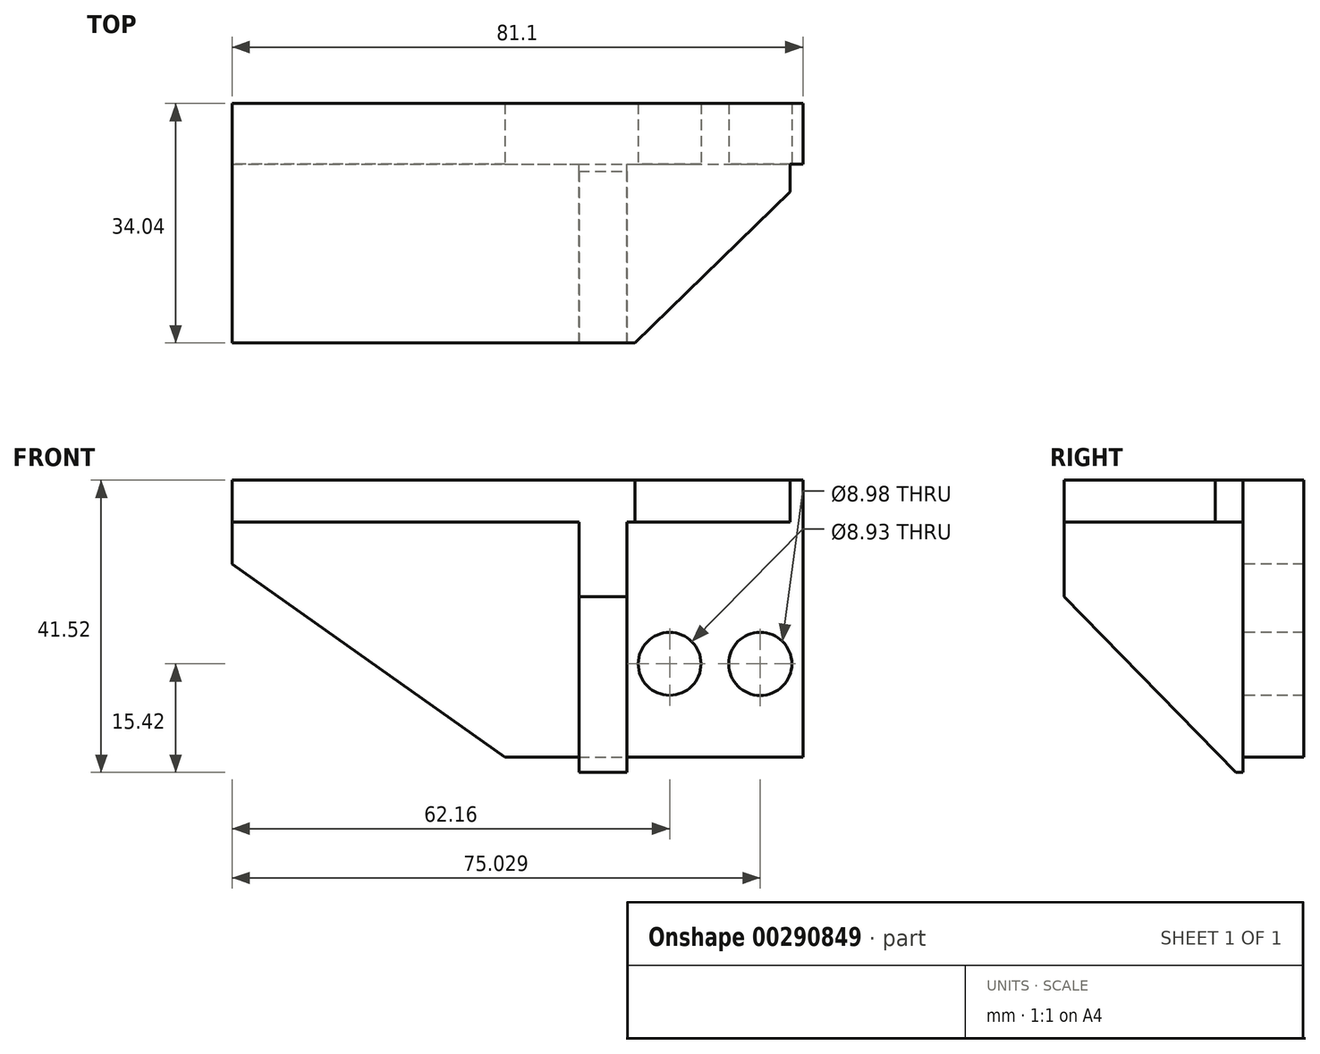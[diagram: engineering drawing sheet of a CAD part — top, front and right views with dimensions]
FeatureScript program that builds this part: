
annotation { "Feature Type Name" : "Feature", "Feature Type Description" : "" }
export const myFeature = defineFeature(function(context is Context, id is Id, definition is map)
    precondition{}
    {
        {
            var Q0;
            Q0=qCreatedBy(makeId("Front.planeOp"),FACE);
            var sketch = newSketch(context, id + "F0", { "sketchPlane" : qUnion([Q0])});
            skLineSegment(sketch, "E0.bottom", {"start": v(-49.3, 26.1) * mm, "end": v(31.8, 26.1) * mm});
            skLineSegment(sketch, "E0.top", {"start": v(-49.3, -13.23) * mm, "end": v(31.8, -13.23) * mm});
            skLineSegment(sketch, "E0.left", {"start": v(-49.3, 26.1) * mm, "end": v(-49.3, -13.23) * mm});
            skLineSegment(sketch, "E0.right", {"start": v(31.8, 26.1) * mm, "end": v(31.8, -13.23) * mm});
            skSolve(sketch);
        }
        {
            var Q0;
            Q0 = qSketchRegion(id + "F0", true);
            extrude(context, id + "F1", {"entities" : qUnion([Q0]), "depth" : 8.64 * mm});
        }
        {
            var Q0;
            Q0=makeQuery(id+"F1.opExtrude","CAP_FACE",FACE,{"disambiguationData":[OSD([sQuery(id+"F0.wireOp",EDGE,"E0.bottom"),sQuery(id+"F0.wireOp",EDGE,"E0.top"),sQuery(id+"F0.wireOp",EDGE,"E0.left"),sQuery(id+"F0.wireOp",EDGE,"E0.right")])],"isStart":false});
            var sketch = newSketch(context, id + "F2", { "sketchPlane" : qUnion([Q0])});
            skLineSegment(sketch, "E1", {"start": v(-8.62, -14.57) * mm, "end": v(-51.6, 15.78) * mm});
            skSolve(sketch);
        }
        {
            var Q0;
            {var subQ0=sQuery(id+"F2.wireOp",EDGE,"E1");var subQ1=makeQuery(id+"F1.opExtrude","CAP_EDGE",EDGE,{"disambiguationData":[OSD([sQuery(id+"F0.wireOp",EDGE,"E0.top")])],"isStart":false});var subQ2=makeQuery(id+"F2.imprint","INTERSECT",VERTEX,{"derivedFrom":[subQ1,subQ0]});Q0=makeQuery(id+"F2.imprint","IMPRINT",FACE,{"disambiguationData":[TD([[makeQuery(id+"F2.imprint","IMPRINT",EDGE,{"disambiguationData":[TD([[subQ2,-1.0]])],"derivedFrom":subQ0}),1.0]])]});}
            extrude(context, id + "F3", {"entities" : qUnion([Q0]), "operationType" : NewBodyOperationType.REMOVE, "oppositeDirection" : true, "depth" : 25.4 * mm});
        }
        {
            var Q0;
            Q0=makeQuery(id+"F1.opExtrude","CAP_FACE",FACE,{"disambiguationData":[OSD([sQuery(id+"F0.wireOp",EDGE,"E0.bottom"),sQuery(id+"F0.wireOp",EDGE,"E0.top"),sQuery(id+"F0.wireOp",EDGE,"E0.left"),sQuery(id+"F0.wireOp",EDGE,"E0.right")])],"isStart":false});
            var sketch = newSketch(context, id + "F4", { "sketchPlane" : qUnion([Q0])});
            skLineSegment(sketch, "E2", {"start": v(-50.14, 20.15) * mm, "end": v(29.99, 20.15) * mm});
            skLineSegment(sketch, "E3", {"start": v(29.99, 20.15) * mm, "end": v(29.99, 26.47) * mm});
            skLineSegment(sketch, "E4", {"start": v(29.99, 26.47) * mm, "end": v(-50.14, 26.47) * mm});
            skLineSegment(sketch, "E5", {"start": v(-50.14, 26.47) * mm, "end": v(-50.14, 20.15) * mm});
            skSolve(sketch);
        }
        {
            var Q0;
            {var subQ5=makeQuery(id+"F1.opExtrude","CAP_EDGE",EDGE,{"disambiguationData":[OSD([sQuery(id+"F0.wireOp",EDGE,"E0.bottom")])],"isStart":false});Q0=makeQuery(id+"F4.imprint","IMPRINT",FACE,{"disambiguationData":[TD([[makeQuery(id+"F4.imprint","IMPRINT",EDGE,{"derivedFrom":subQ5}),-1.0]])]});}
            extrude(context, id + "F5", {"entities" : qUnion([Q0]), "operationType" : NewBodyOperationType.ADD, "depth" : 25.4 * mm});
        }
        {
            var Q0;
            Q0=makeQuery(id+"F1.opExtrude","CAP_FACE",FACE,{"disambiguationData":[OSD([sQuery(id+"F0.wireOp",EDGE,"E0.bottom"),sQuery(id+"F0.wireOp",EDGE,"E0.top"),sQuery(id+"F0.wireOp",EDGE,"E0.left"),sQuery(id+"F0.wireOp",EDGE,"E0.right")])],"isStart":false});
            var sketch = newSketch(context, id + "F6", { "sketchPlane" : qUnion([Q0])});
            skLineSegment(sketch, "E6", {"start": v(0, 20.15) * mm, "end": v(0, -15.42) * mm});
            skLineSegment(sketch, "E7", {"start": v(0, -15.42) * mm, "end": v(6.8, -15.42) * mm});
            skLineSegment(sketch, "E8", {"start": v(6.8, -15.42) * mm, "end": v(6.8, 20.15) * mm});
            skLineSegment(sketch, "E9", {"start": v(6.8, 20.15) * mm, "end": v(0, 20.15) * mm});
            skSolve(sketch);
        }
        {
            var Q0;
            Q0 = qSketchRegion(id + "F6", true);
            extrude(context, id + "F7", {"entities" : qUnion([Q0]), "operationType" : NewBodyOperationType.ADD, "depth" : 25.4 * mm});
        }
        {
            var Q0;
            Q0=makeQuery(id+"F7.opExtrude","SWEPT_FACE",FACE,{"disambiguationData":[OSD([sQuery(id+"F6.wireOp",EDGE,"E8")])]});
            var sketch = newSketch(context, id + "F8", { "sketchPlane" : qUnion([Q0])});
            skLineSegment(sketch, "E10", {"start": v(-8.13, -17) * mm, "end": v(-37.03, 12.63) * mm});
            skSolve(sketch);
        }
        {
            var Q0;
            {var subQ0=sQuery(id+"F8.wireOp",EDGE,"E10");var subQ1=sQuery(id+"F6.wireOp",EDGE,"E8");var subQ4=makeQuery(id+"F7.opExtrude","CAP_EDGE",EDGE,{"disambiguationData":[OSD([subQ1])],"isStart":false});var subQ5=makeQuery(id+"F8.imprint","INTERSECT",VERTEX,{"derivedFrom":[subQ4,subQ0]});Q0=makeQuery(id+"F8.imprint","IMPRINT",FACE,{"disambiguationData":[TD([[makeQuery(id+"F8.imprint","IMPRINT",EDGE,{"disambiguationData":[TD([[subQ5,1.0]])],"derivedFrom":subQ0}),1.0]])]});}
            extrude(context, id + "F9", {"entities" : qUnion([Q0]), "operationType" : NewBodyOperationType.REMOVE, "oppositeDirection" : true, "depth" : 25.4 * mm});
        }
        {
            var Q0;
            {var subQ0=sQuery(id+"F0.wireOp",EDGE,"E0.top");var subQ1=sQuery(id+"F0.wireOp",EDGE,"E0.right");var subQ2=sQuery(id+"F0.wireOp",EDGE,"E0.bottom");Q0=makeQuery(id+"F7.boolean.opBoolean","SPLIT",FACE,{"disambiguationData":[TD([makeQuery(id+"F1.opExtrude","SWEPT_FACE",FACE,{"disambiguationData":[OSD([subQ2])]})])],"derivedFrom":makeQuery(id+"F1.opExtrude","CAP_FACE",FACE,{"disambiguationData":[OSD([subQ2,subQ0,sQuery(id+"F0.wireOp",EDGE,"E0.left"),subQ1])],"isStart":false})});}
            var sketch = newSketch(context, id + "F10", { "sketchPlane" : qUnion([Q0])});
            skCircle(sketch, "E11", {"center": v(12.87, 0) * mm, "radius": 4.46 * mm});
            skCircle(sketch, "E12", {"center": v(25.74, 0) * mm, "radius": 4.5 * mm});
            skSolve(sketch);
        }
        {
            var Q0;
            Q0 = qSketchRegion(id + "F10", true);
            extrude(context, id + "F11", {"entities" : qUnion([Q0]), "operationType" : NewBodyOperationType.REMOVE, "oppositeDirection" : true, "depth" : 25.4 * mm});
        }
        {
            var Q0;
            {var subQ0=sQuery(id+"F0.wireOp",EDGE,"E0.bottom");Q0=makeQuery(id+"F5.boolean.opBoolean","MERGE",FACE,{"derivedFrom":[makeQuery(id+"F1.opExtrude","SWEPT_FACE",FACE,{"disambiguationData":[OSD([subQ0])]}),makeQuery(id+"F5.opExtrude","SWEPT_FACE",FACE,{"disambiguationData":[OSD([subQ0])]})]});}
            var sketch = newSketch(context, id + "F12", { "sketchPlane" : qUnion([Q0])});
            skLineSegment(sketch, "E13", {"start": v(31.8, -10.77) * mm, "end": v(2.91, -38.94) * mm});
            skSolve(sketch);
        }
        {
            var Q0;
            {var subQ0=sQuery(id+"F12.wireOp",EDGE,"E13");var subQ1=sQuery(id+"F0.wireOp",EDGE,"E0.bottom");var subQ4=makeQuery(id+"F5.opExtrude","CAP_EDGE",EDGE,{"disambiguationData":[OSD([subQ1])],"isStart":false});var subQ5=makeQuery(id+"F12.imprint","INTERSECT",VERTEX,{"derivedFrom":[subQ4,subQ0]});Q0=makeQuery(id+"F12.imprint","IMPRINT",FACE,{"disambiguationData":[TD([[makeQuery(id+"F12.imprint","IMPRINT",EDGE,{"disambiguationData":[TD([[subQ5,1.0]])],"derivedFrom":subQ0}),1.0]])]});}
            extrude(context, id + "F13", {"entities" : qUnion([Q0]), "operationType" : NewBodyOperationType.REMOVE, "oppositeDirection" : true, "depth" : 25.4 * mm});
        }
    });
